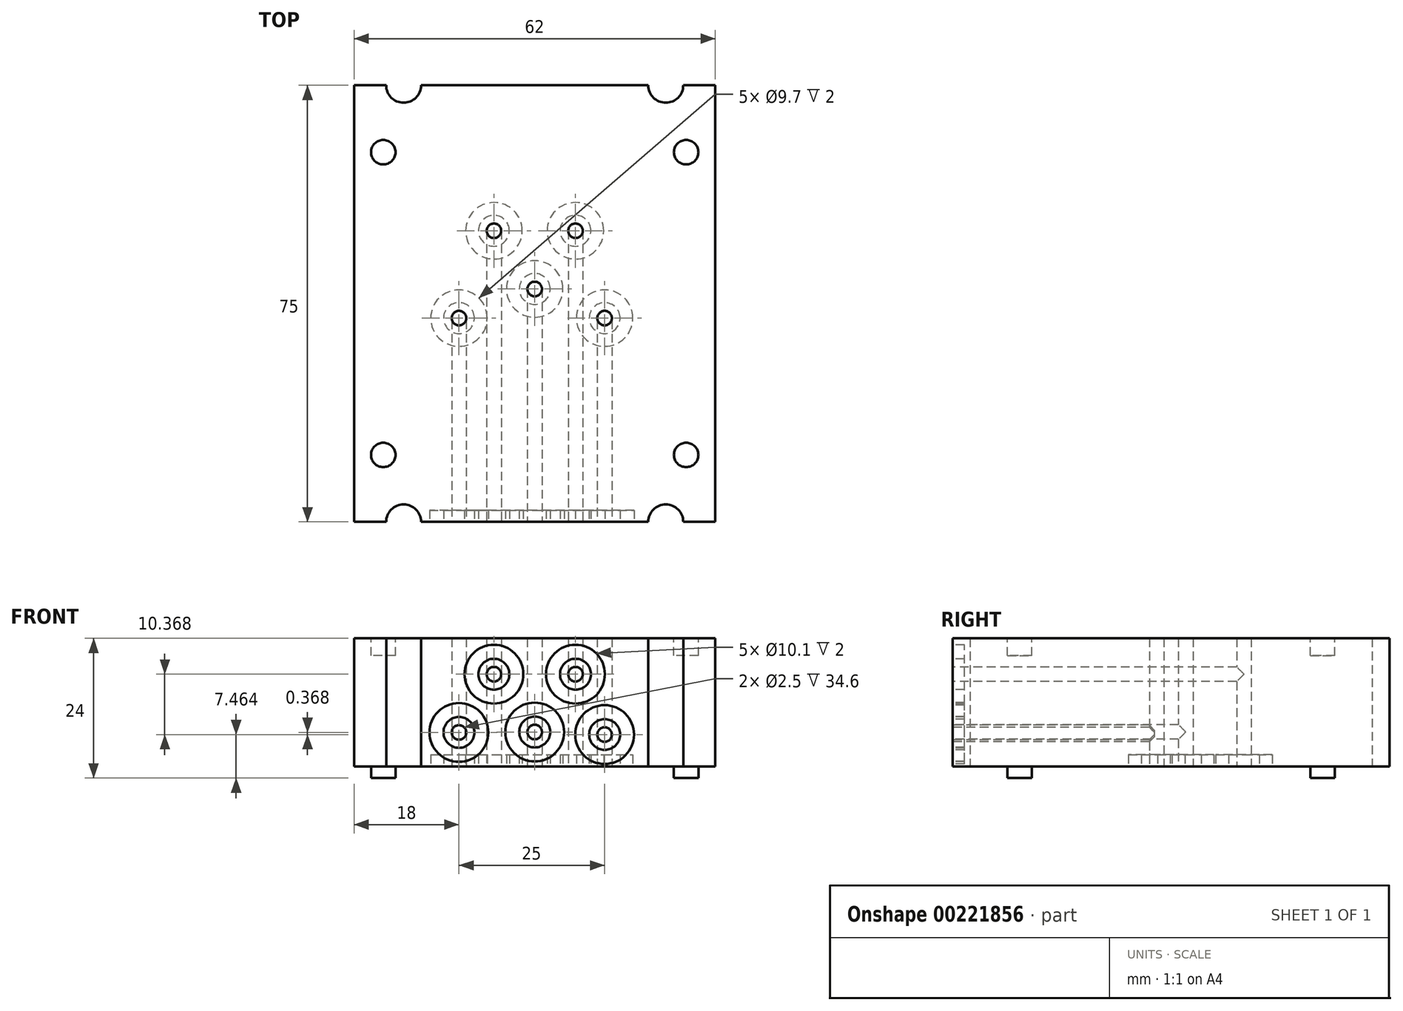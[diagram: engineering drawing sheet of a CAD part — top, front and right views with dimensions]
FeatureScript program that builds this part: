
annotation { "Feature Type Name" : "Feature", "Feature Type Description" : "" }
export const myFeature = defineFeature(function(context is Context, id is Id, definition is map)
    precondition{}
    {
        {
            var Q0;
            Q0=qCreatedBy(makeId("Top.planeOp"),FACE);
            var sketch = newSketch(context, id + "F0", { "sketchPlane" : qUnion([Q0])});
            skLineSegment(sketch, "E0.bottom", {"start": v(-31, 37.5) * mm, "end": v(31, 37.5) * mm});
            skLineSegment(sketch, "E0.top", {"start": v(-31, -37.5) * mm, "end": v(31, -37.5) * mm});
            skLineSegment(sketch, "E0.left", {"start": v(-31, 37.5) * mm, "end": v(-31, -37.5) * mm});
            skLineSegment(sketch, "E0.right", {"start": v(31, 37.5) * mm, "end": v(31, -37.5) * mm});
            skPoint(sketch, "E0.middle", {"position": v(0, 0) * mm});
            skSolve(sketch);
        }
        {
            var Q0;
            Q0=makeQuery(id+"F0.imprint","IMPRINT",FACE,{"disambiguationData":[TD([[makeQuery(id+"F0.imprint","IMPRINT",EDGE,{"derivedFrom":sQuery(id+"F0.wireOp",EDGE,"E0.bottom")}),-1.0]])]});
            extrude(context, id + "F1", {"entities" : qUnion([Q0]), "depth" : 14 * mm});
        }
        {
            var Q0;
            Q0=makeQuery(id+"F1.opExtrude","CAP_FACE",FACE,{"disambiguationData":[OSD([sQuery(id+"F0.wireOp",EDGE,"E0.bottom"),sQuery(id+"F0.wireOp",EDGE,"E0.top"),sQuery(id+"F0.wireOp",EDGE,"E0.left"),sQuery(id+"F0.wireOp",EDGE,"E0.right")])],"isStart":true});
            var sketch = newSketch(context, id + "F2", { "sketchPlane" : qUnion([Q0])});
            skLineSegment(sketch, "E1.bottom", {"start": v(-31, 37.5) * mm, "end": v(31, 37.5) * mm});
            skLineSegment(sketch, "E1.top", {"start": v(-31, -37.5) * mm, "end": v(31, -37.5) * mm});
            skLineSegment(sketch, "E1.left", {"start": v(-31, 37.5) * mm, "end": v(-31, -37.5) * mm});
            skLineSegment(sketch, "E1.right", {"start": v(31, 37.5) * mm, "end": v(31, -37.5) * mm});
            skPoint(sketch, "E1.middle", {"position": v(0, 0) * mm});
            skSolve(sketch);
        }
        {
            var Q0;
            Q0=qSketchRegion(id+"F2",true);
            extrude(context, id + "F3", {"entities" : qUnion([Q0]), "operationType" : NewBodyOperationType.ADD, "depth" : 8 * mm});
        }
        {
            var Q0;
            Q0=makeQuery(id+"F3.opExtrude","CAP_FACE",FACE,{"disambiguationData":[OSD([sQuery(id+"F2.wireOp",EDGE,"E1.bottom"),sQuery(id+"F2.wireOp",EDGE,"E1.top"),sQuery(id+"F2.wireOp",EDGE,"E1.left"),sQuery(id+"F2.wireOp",EDGE,"E1.right")])],"isStart":false});
            var sketch = newSketch(context, id + "F4", { "sketchPlane" : qUnion([Q0])});
            skCircle(sketch, "E2", {"center": v(-13, 2.5) * mm, "radius": 1.25 * mm});
            skCircle(sketch, "E3", {"center": v(-7, -12.5) * mm, "radius": 1.25 * mm});
            skCircle(sketch, "E4", {"center": v(12, 2.5) * mm, "radius": 1.25 * mm});
            skCircle(sketch, "E5", {"center": v(7, -12.5) * mm, "radius": 1.25 * mm});
            skCircle(sketch, "E6", {"center": v(0, -2.5) * mm, "radius": 1.25 * mm});
            skSolve(sketch);
        }
        {
            var Q0;
            Q0=makeQuery(id+"F4.imprint","IMPRINT",FACE,{"disambiguationData":[TD([[makeQuery(id+"F4.imprint","IMPRINT",EDGE,{"derivedFrom":sQuery(id+"F4.wireOp",EDGE,"E2")}),1.0]])]});
            var Q1;
            Q1=makeQuery(id+"F4.imprint","IMPRINT",FACE,{"disambiguationData":[TD([[makeQuery(id+"F4.imprint","IMPRINT",EDGE,{"derivedFrom":sQuery(id+"F4.wireOp",EDGE,"E3")}),1.0]])]});
            var Q2;
            Q2=makeQuery(id+"F4.imprint","IMPRINT",FACE,{"disambiguationData":[TD([[makeQuery(id+"F4.imprint","IMPRINT",EDGE,{"derivedFrom":sQuery(id+"F4.wireOp",EDGE,"E6")}),1.0]])]});
            var Q3;
            Q3=makeQuery(id+"F4.imprint","IMPRINT",FACE,{"disambiguationData":[TD([[makeQuery(id+"F4.imprint","IMPRINT",EDGE,{"derivedFrom":sQuery(id+"F4.wireOp",EDGE,"E5")}),1.0]])]});
            var Q4;
            Q4=makeQuery(id+"F4.imprint","IMPRINT",FACE,{"disambiguationData":[TD([[makeQuery(id+"F4.imprint","IMPRINT",EDGE,{"derivedFrom":sQuery(id+"F4.wireOp",EDGE,"E4")}),1.0]])]});
            extrude(context, id + "F5", {"entities" : qUnion([Q0, Q1, Q2, Q3, Q4]), "operationType" : NewBodyOperationType.REMOVE, "oppositeDirection" : true, "depth" : 38 * mm});
        }
        {
            var Q0;
            Q0=makeQuery(id+"F3.opExtrude","CAP_FACE",FACE,{"disambiguationData":[OSD([sQuery(id+"F2.wireOp",EDGE,"E1.bottom"),sQuery(id+"F2.wireOp",EDGE,"E1.top"),sQuery(id+"F2.wireOp",EDGE,"E1.left"),sQuery(id+"F2.wireOp",EDGE,"E1.right")])],"isStart":false});
            var sketch = newSketch(context, id + "F6", { "sketchPlane" : qUnion([Q0])});
            skCircle(sketch, "E7", {"center": v(-7, -12.5) * mm, "radius": 2.65 * mm});
            skCircle(sketch, "E8", {"center": v(-7, -12.5) * mm, "radius": 4.85 * mm});
            skCircle(sketch, "E9", {"center": v(-13, 2.5) * mm, "radius": 2.65 * mm});
            skCircle(sketch, "E10", {"center": v(-13, 2.5) * mm, "radius": 4.85 * mm});
            skCircle(sketch, "E11", {"center": v(0, -2.5) * mm, "radius": 2.65 * mm});
            skCircle(sketch, "E12", {"center": v(0, -2.5) * mm, "radius": 4.85 * mm});
            skCircle(sketch, "E13", {"center": v(12, 2.5) * mm, "radius": 2.65 * mm});
            skCircle(sketch, "E14", {"center": v(12, 2.5) * mm, "radius": 4.85 * mm});
            skCircle(sketch, "E15", {"center": v(7, -12.5) * mm, "radius": 2.65 * mm});
            skCircle(sketch, "E16", {"center": v(7, -12.5) * mm, "radius": 4.85 * mm});
            skSolve(sketch);
        }
        {
            var Q0;
            Q0=makeQuery(id+"F6.imprint","IMPRINT",FACE,{"disambiguationData":[TD([[makeQuery(id+"F6.imprint","IMPRINT",EDGE,{"derivedFrom":sQuery(id+"F6.wireOp",EDGE,"E7")}),-1.0]])]});
            var Q1;
            Q1=makeQuery(id+"F6.imprint","IMPRINT",FACE,{"disambiguationData":[TD([[makeQuery(id+"F6.imprint","IMPRINT",EDGE,{"derivedFrom":sQuery(id+"F6.wireOp",EDGE,"E9")}),-1.0]])]});
            var Q2;
            Q2=makeQuery(id+"F6.imprint","IMPRINT",FACE,{"disambiguationData":[TD([[makeQuery(id+"F6.imprint","IMPRINT",EDGE,{"derivedFrom":sQuery(id+"F6.wireOp",EDGE,"E11")}),-1.0]])]});
            var Q3;
            Q3=makeQuery(id+"F6.imprint","IMPRINT",FACE,{"disambiguationData":[TD([[makeQuery(id+"F6.imprint","IMPRINT",EDGE,{"derivedFrom":sQuery(id+"F6.wireOp",EDGE,"E13")}),-1.0]])]});
            var Q4;
            Q4=makeQuery(id+"F6.imprint","IMPRINT",FACE,{"disambiguationData":[TD([[makeQuery(id+"F6.imprint","IMPRINT",EDGE,{"derivedFrom":sQuery(id+"F6.wireOp",EDGE,"E15")}),-1.0]])]});
            extrude(context, id + "F7", {"entities" : qUnion([Q0, Q1, Q2, Q3, Q4]), "operationType" : NewBodyOperationType.REMOVE, "oppositeDirection" : true, "depth" : 2 * mm});
        }
        {
            var Q0;
            Q0=makeQuery(id+"F1.opExtrude","CAP_FACE",FACE,{"disambiguationData":[OSD([sQuery(id+"F0.wireOp",EDGE,"E0.bottom"),sQuery(id+"F0.wireOp",EDGE,"E0.top"),sQuery(id+"F0.wireOp",EDGE,"E0.left"),sQuery(id+"F0.wireOp",EDGE,"E0.right")])],"isStart":false});
            var sketch = newSketch(context, id + "F8", { "sketchPlane" : qUnion([Q0])});
            skCircle(sketch, "E17", {"center": v(-26, 26) * mm, "radius": 2.1 * mm});
            skCircle(sketch, "E18", {"center": v(-26, -26) * mm, "radius": 2.1 * mm});
            skCircle(sketch, "E19", {"center": v(26, -26) * mm, "radius": 2.1 * mm});
            skCircle(sketch, "E20", {"center": v(26, 26) * mm, "radius": 2.1 * mm});
            skSolve(sketch);
        }
        {
            var Q0;
            Q0=makeQuery(id+"F3.boolean.opBoolean","MERGE",FACE,{"derivedFrom":[makeQuery(id+"F1.opExtrude","SWEPT_FACE",FACE,{"disambiguationData":[OSD([sQuery(id+"F0.wireOp",EDGE,"E0.top")])]}),makeQuery(id+"F3.opExtrude","SWEPT_FACE",FACE,{"disambiguationData":[OSD([sQuery(id+"F2.wireOp",EDGE,"E1.bottom")])]})]});
            var sketch = newSketch(context, id + "F9", { "sketchPlane" : qUnion([Q0])});
            skCircle(sketch, "E21", {"center": v(12, -2.54) * mm, "radius": 1.25 * mm});
            skCircle(sketch, "E22", {"center": v(7, 7.83) * mm, "radius": 1.25 * mm});
            skCircle(sketch, "E23", {"center": v(0, -2.1) * mm, "radius": 1.25 * mm});
            skCircle(sketch, "E24", {"center": v(-7, 7.83) * mm, "radius": 1.25 * mm});
            skCircle(sketch, "E25", {"center": v(-13, -2.17) * mm, "radius": 1.25 * mm});
            skSolve(sketch);
        }
        {
            var Q0;
            Q0=makeQuery(id+"F9.imprint","IMPRINT",FACE,{"disambiguationData":[TD([[makeQuery(id+"F9.imprint","IMPRINT",EDGE,{"derivedFrom":sQuery(id+"F9.wireOp",EDGE,"E24")}),1.0]])]});
            var Q1;
            Q1=makeQuery(id+"F9.imprint","IMPRINT",FACE,{"disambiguationData":[TD([[makeQuery(id+"F9.imprint","IMPRINT",EDGE,{"derivedFrom":sQuery(id+"F9.wireOp",EDGE,"E22")}),1.0]])]});
            extrude(context, id + "F10", {"entities" : qUnion([Q0, Q1]), "operationType" : NewBodyOperationType.REMOVE, "oppositeDirection" : true, "depth" : 50 * mm});
        }
        {
            var Q0;
            Q0=makeQuery(id+"F3.boolean.opBoolean","MERGE",FACE,{"derivedFrom":[makeQuery(id+"F1.opExtrude","SWEPT_FACE",FACE,{"disambiguationData":[OSD([sQuery(id+"F0.wireOp",EDGE,"E0.top")])]}),makeQuery(id+"F3.opExtrude","SWEPT_FACE",FACE,{"disambiguationData":[OSD([sQuery(id+"F2.wireOp",EDGE,"E1.bottom")])]})]});
            var sketch = newSketch(context, id + "F11", { "sketchPlane" : qUnion([Q0])});
            skCircle(sketch, "E26", {"center": v(-7, 7.83) * mm, "radius": 5.05 * mm});
            skCircle(sketch, "E27", {"center": v(-13, -2.17) * mm, "radius": 5.05 * mm});
            skCircle(sketch, "E28", {"center": v(0, -2.1) * mm, "radius": 5.05 * mm});
            skCircle(sketch, "E29", {"center": v(12, -2.54) * mm, "radius": 5.05 * mm});
            skCircle(sketch, "E30", {"center": v(7, 7.83) * mm, "radius": 5.05 * mm});
            skCircle(sketch, "E31", {"center": v(-7, 7.83) * mm, "radius": 2.65 * mm});
            skCircle(sketch, "E32", {"center": v(-13, -2.17) * mm, "radius": 2.65 * mm});
            skCircle(sketch, "E33", {"center": v(0, -2.1) * mm, "radius": 2.65 * mm});
            skCircle(sketch, "E34", {"center": v(12, -2.54) * mm, "radius": 2.65 * mm});
            skCircle(sketch, "E35", {"center": v(7, 7.83) * mm, "radius": 2.65 * mm});
            skSolve(sketch);
        }
        {
            var Q0;
            Q0=makeQuery(id+"F11.imprint","IMPRINT",FACE,{"disambiguationData":[TD([[makeQuery(id+"F11.imprint","IMPRINT",EDGE,{"derivedFrom":sQuery(id+"F11.wireOp",EDGE,"E26")}),1.0]])]});
            var Q1;
            Q1=makeQuery(id+"F11.imprint","IMPRINT",FACE,{"disambiguationData":[TD([[makeQuery(id+"F11.imprint","IMPRINT",EDGE,{"derivedFrom":sQuery(id+"F11.wireOp",EDGE,"E27")}),1.0]])]});
            var Q2;
            Q2=makeQuery(id+"F11.imprint","IMPRINT",FACE,{"disambiguationData":[TD([[makeQuery(id+"F11.imprint","IMPRINT",EDGE,{"derivedFrom":sQuery(id+"F11.wireOp",EDGE,"E28")}),1.0]])]});
            var Q3;
            Q3=makeQuery(id+"F11.imprint","IMPRINT",FACE,{"disambiguationData":[TD([[makeQuery(id+"F11.imprint","IMPRINT",EDGE,{"derivedFrom":sQuery(id+"F11.wireOp",EDGE,"E29")}),1.0]])]});
            var Q4;
            Q4=makeQuery(id+"F11.imprint","IMPRINT",FACE,{"disambiguationData":[TD([[makeQuery(id+"F11.imprint","IMPRINT",EDGE,{"derivedFrom":sQuery(id+"F11.wireOp",EDGE,"E30")}),1.0]])]});
            extrude(context, id + "F12", {"entities" : qUnion([Q0, Q1, Q2, Q3, Q4]), "operationType" : NewBodyOperationType.REMOVE, "oppositeDirection" : true, "depth" : 2 * mm});
        }
        {
            var Q0;
            Q0=makeQuery(id+"F9.imprint","IMPRINT",FACE,{"disambiguationData":[TD([[makeQuery(id+"F9.imprint","IMPRINT",EDGE,{"derivedFrom":sQuery(id+"F9.wireOp",EDGE,"E23")}),1.0]])]});
            extrude(context, id + "F13", {"entities" : qUnion([Q0]), "operationType" : NewBodyOperationType.REMOVE, "oppositeDirection" : true, "depth" : 40 * mm});
        }
        {
            var Q0;
            Q0=makeQuery(id+"F9.imprint","IMPRINT",FACE,{"disambiguationData":[TD([[makeQuery(id+"F9.imprint","IMPRINT",EDGE,{"derivedFrom":sQuery(id+"F9.wireOp",EDGE,"E21")}),1.0]])]});
            var Q1;
            Q1=makeQuery(id+"F9.imprint","IMPRINT",FACE,{"disambiguationData":[TD([[makeQuery(id+"F9.imprint","IMPRINT",EDGE,{"derivedFrom":sQuery(id+"F9.wireOp",EDGE,"E25")}),1.0]])]});
            extrude(context, id + "F14", {"entities" : qUnion([Q0, Q1]), "operationType" : NewBodyOperationType.REMOVE, "oppositeDirection" : true, "depth" : 34.6 * mm});
        }
        {
            var Q0;
            {var subQ0=sQuery(id+"F2.wireOp",EDGE,"E1.right");var subQ1=sQuery(id+"F2.wireOp",EDGE,"E1.left");var subQ2=sQuery(id+"F2.wireOp",EDGE,"E1.top");var subQ3=sQuery(id+"F2.wireOp",EDGE,"E1.bottom");Q0=makeQuery(id+"F7.boolean.opBoolean","SPLIT",FACE,{"disambiguationData":[TD([makeQuery(id+"F1.opExtrude","SWEPT_FACE",FACE,{"disambiguationData":[OSD([sQuery(id+"F0.wireOp",EDGE,"E0.bottom")])]})])],"derivedFrom":makeQuery(id+"F3.opExtrude","CAP_FACE",FACE,{"disambiguationData":[OSD([subQ3,subQ2,subQ1,subQ0])],"isStart":false})});}
            var sketch = newSketch(context, id + "F15", { "sketchPlane" : qUnion([Q0])});
            skCircle(sketch, "E36", {"center": v(-22.5, 37.5) * mm, "radius": 3 * mm});
            skCircle(sketch, "E37", {"center": v(22.5, 37.5) * mm, "radius": 3 * mm});
            skCircle(sketch, "E38", {"center": v(-22.5, -37.5) * mm, "radius": 3 * mm});
            skCircle(sketch, "E39", {"center": v(22.5, -37.5) * mm, "radius": 3 * mm});
            skSolve(sketch);
        }
        {
            var Q0;
            {var subQ0=sQuery(id+"F15.wireOp",EDGE,"E36");var subQ1=makeQuery(id+"F3.opExtrude","CAP_EDGE",EDGE,{"disambiguationData":[OSD([sQuery(id+"F2.wireOp",EDGE,"E1.bottom")])],"isStart":false});var subQ2=makeQuery(id+"F15.imprint","INTERSECT",VERTEX,{"disambiguationData":[OD(0.0)],"derivedFrom":[subQ1,subQ0]});Q0=makeQuery(id+"F15.imprint","IMPRINT",FACE,{"disambiguationData":[TD([[makeQuery(id+"F15.imprint","IMPRINT",EDGE,{"disambiguationData":[TD([[subQ2,-1.0]])],"derivedFrom":subQ0}),1.0]])]});}
            var Q1;
            {var subQ0=sQuery(id+"F15.wireOp",EDGE,"E37");var subQ1=makeQuery(id+"F3.opExtrude","CAP_EDGE",EDGE,{"disambiguationData":[OSD([sQuery(id+"F2.wireOp",EDGE,"E1.bottom")])],"isStart":false});var subQ2=makeQuery(id+"F15.imprint","INTERSECT",VERTEX,{"disambiguationData":[OD(0.0)],"derivedFrom":[subQ1,subQ0]});Q1=makeQuery(id+"F15.imprint","IMPRINT",FACE,{"disambiguationData":[TD([[makeQuery(id+"F15.imprint","IMPRINT",EDGE,{"disambiguationData":[TD([[subQ2,1.0]])],"derivedFrom":subQ0}),1.0]])]});}
            var Q2;
            {var subQ0=sQuery(id+"F15.wireOp",EDGE,"E38");var subQ1=makeQuery(id+"F3.opExtrude","CAP_EDGE",EDGE,{"disambiguationData":[OSD([sQuery(id+"F2.wireOp",EDGE,"E1.top")])],"isStart":false});var subQ2=makeQuery(id+"F15.imprint","INTERSECT",VERTEX,{"disambiguationData":[OD(0.0)],"derivedFrom":[subQ1,subQ0]});Q2=makeQuery(id+"F15.imprint","IMPRINT",FACE,{"disambiguationData":[TD([[makeQuery(id+"F15.imprint","IMPRINT",EDGE,{"disambiguationData":[TD([[subQ2,1.0]])],"derivedFrom":subQ0}),1.0]])]});}
            var Q3;
            {var subQ0=sQuery(id+"F15.wireOp",EDGE,"E39");var subQ1=makeQuery(id+"F3.opExtrude","CAP_EDGE",EDGE,{"disambiguationData":[OSD([sQuery(id+"F2.wireOp",EDGE,"E1.top")])],"isStart":false});var subQ2=makeQuery(id+"F15.imprint","INTERSECT",VERTEX,{"disambiguationData":[OD(0.0)],"derivedFrom":[subQ1,subQ0]});Q3=makeQuery(id+"F15.imprint","IMPRINT",FACE,{"disambiguationData":[TD([[makeQuery(id+"F15.imprint","IMPRINT",EDGE,{"disambiguationData":[TD([[subQ2,-1.0]])],"derivedFrom":subQ0}),1.0]])]});}
            extrude(context, id + "F16", {"entities" : qUnion([Q0, Q1, Q2, Q3]), "operationType" : NewBodyOperationType.REMOVE, "oppositeDirection" : true, "depth" : 22 * mm});
        }
        {
            var Q0;
            Q0 = qSketchRegion(id + "F8", true);
            extrude(context, id + "F17", {"entities" : qUnion([Q0]), "operationType" : NewBodyOperationType.REMOVE, "oppositeDirection" : true, "depth" : 3 * mm});
        }
        {
            var Q0;
            {var subQ0=sQuery(id+"F2.wireOp",EDGE,"E1.right");var subQ1=sQuery(id+"F2.wireOp",EDGE,"E1.left");var subQ2=sQuery(id+"F2.wireOp",EDGE,"E1.top");var subQ3=sQuery(id+"F2.wireOp",EDGE,"E1.bottom");Q0=makeQuery(id+"F7.boolean.opBoolean","SPLIT",FACE,{"disambiguationData":[TD([makeQuery(id+"F1.opExtrude","SWEPT_FACE",FACE,{"disambiguationData":[OSD([sQuery(id+"F0.wireOp",EDGE,"E0.bottom")])]})])],"derivedFrom":makeQuery(id+"F3.opExtrude","CAP_FACE",FACE,{"disambiguationData":[OSD([subQ3,subQ2,subQ1,subQ0])],"isStart":false})});}
            var sketch = newSketch(context, id + "F18", { "sketchPlane" : qUnion([Q0])});
            skCircle(sketch, "E40", {"center": v(-26, -26) * mm, "radius": 2.1 * mm});
            skCircle(sketch, "E41", {"center": v(-26, 26) * mm, "radius": 2.1 * mm});
            skCircle(sketch, "E42", {"center": v(26, 26) * mm, "radius": 2.1 * mm});
            skCircle(sketch, "E43", {"center": v(26, -26) * mm, "radius": 2.1 * mm});
            skSolve(sketch);
        }
        {
            var Q0;
            Q0=makeQuery(id+"F18.imprint","IMPRINT",FACE,{"disambiguationData":[TD([[makeQuery(id+"F18.imprint","IMPRINT",EDGE,{"derivedFrom":sQuery(id+"F18.wireOp",EDGE,"E41")}),1.0]])]});
            var Q1;
            Q1=makeQuery(id+"F18.imprint","IMPRINT",FACE,{"disambiguationData":[TD([[makeQuery(id+"F18.imprint","IMPRINT",EDGE,{"derivedFrom":sQuery(id+"F18.wireOp",EDGE,"E42")}),1.0]])]});
            var Q2;
            Q2=makeQuery(id+"F18.imprint","IMPRINT",FACE,{"disambiguationData":[TD([[makeQuery(id+"F18.imprint","IMPRINT",EDGE,{"derivedFrom":sQuery(id+"F18.wireOp",EDGE,"E43")}),1.0]])]});
            var Q3;
            Q3=makeQuery(id+"F18.imprint","IMPRINT",FACE,{"disambiguationData":[TD([[makeQuery(id+"F18.imprint","IMPRINT",EDGE,{"derivedFrom":sQuery(id+"F18.wireOp",EDGE,"E40")}),1.0]])]});
            extrude(context, id + "F19", {"entities" : qUnion([Q0, Q1, Q2, Q3]), "operationType" : NewBodyOperationType.ADD, "depth" : 2 * mm});
        }
    });
